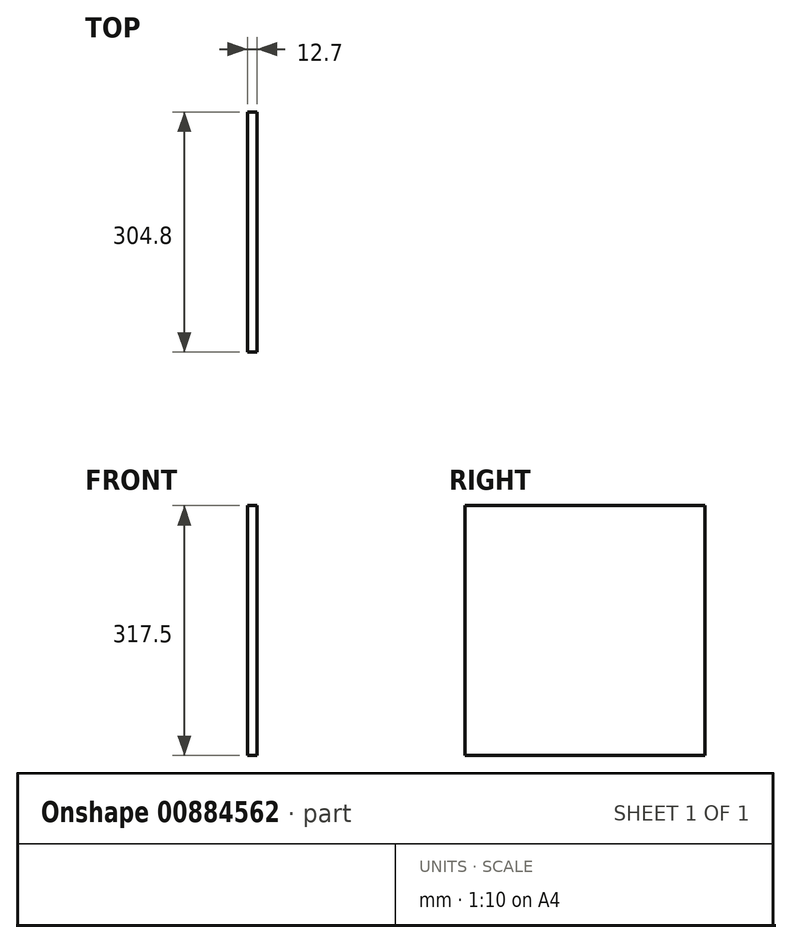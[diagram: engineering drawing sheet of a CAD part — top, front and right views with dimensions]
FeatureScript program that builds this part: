
annotation { "Feature Type Name" : "Feature", "Feature Type Description" : "" }
export const myFeature = defineFeature(function(context is Context, id is Id, definition is map)
    precondition{}
    {
        {
            var Q0;
            Q0=qCreatedBy(makeId("Right.planeOp"),FACE);
            var sketch = newSketch(context, id + "F0", { "sketchPlane" : qUnion([Q0])});
            skLineSegment(sketch, "E0.bottom", {"start": v(152.4, -158.75) * mm, "end": v(-152.4, -158.75) * mm});
            skLineSegment(sketch, "E0.top", {"start": v(152.4, 158.75) * mm, "end": v(-152.4, 158.75) * mm});
            skLineSegment(sketch, "E0.left", {"start": v(152.4, -158.75) * mm, "end": v(152.4, 158.75) * mm});
            skLineSegment(sketch, "E0.right", {"start": v(-152.4, -158.75) * mm, "end": v(-152.4, 158.75) * mm});
            skPoint(sketch, "E0.middle", {"position": v(0, 0) * mm});
            skSolve(sketch);
        }
        {
            var Q0;
            Q0 = qSketchRegion(id + "F0", true);
            extrude(context, id + "F1", {"entities" : qUnion([Q0]), "endBound" : BoundingType.SYMMETRIC, "depth" : 12.7 * mm, "offsetDistance" : 25.4 * mm});
        }
    });
